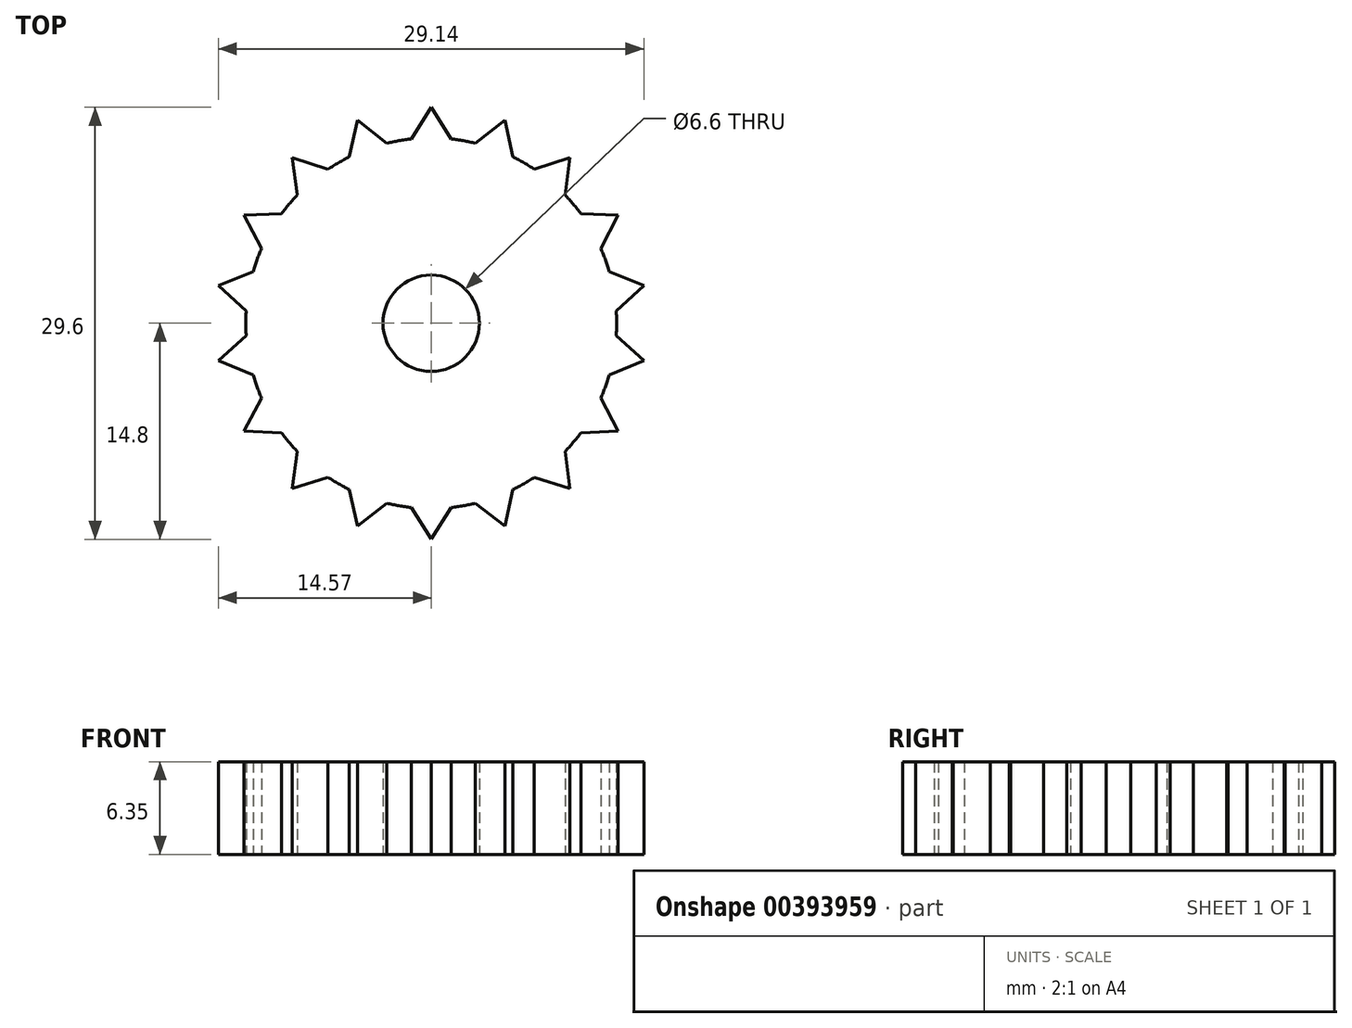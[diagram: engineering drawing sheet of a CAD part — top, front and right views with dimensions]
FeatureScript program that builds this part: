
annotation { "Feature Type Name" : "Feature", "Feature Type Description" : "" }
export const myFeature = defineFeature(function(context is Context, id is Id, definition is map)
    precondition{}
    {
        {
            var Q0;
            Q0=qCreatedBy(makeId("Top.planeOp"),FACE);
            var sketch = newSketch(context, id + "F0", { "sketchPlane" : qUnion([Q0])});
            skCircle(sketch, "E0", {"center": v(0, 0) * mm, "radius": 12.7 * mm});
            skCircle(sketch, "E1", {"center": v(0, 0) * mm, "radius": 3.3 * mm});
            skLineSegment(sketch, "E2", {"start": v(0, 12.7) * mm, "end": v(0, 14.8) * mm});
            skLineSegment(sketch, "E3", {"start": v(0, 14.8) * mm, "end": v(-1.37, 12.63) * mm});
            skLineSegment(sketch, "E4", {"start": v(0, 14.8) * mm, "end": v(1.37, 12.63) * mm});
            skLineSegment(sketch, "E5.1.0", {"start": v(-5.06, 13.9) * mm, "end": v(-5.6, 11.4) * mm});
            skLineSegment(sketch, "E5.1.1", {"start": v(-5.06, 13.9) * mm, "end": v(-3.03, 12.33) * mm});
            skLineSegment(sketch, "E5.2.0", {"start": v(-9.51, 11.33) * mm, "end": v(-9.16, 8.8) * mm});
            skLineSegment(sketch, "E5.2.1", {"start": v(-9.51, 11.33) * mm, "end": v(-7.07, 10.55) * mm});
            skLineSegment(sketch, "E5.3.0", {"start": v(-12.81, 7.4) * mm, "end": v(-11.62, 5.13) * mm});
            skLineSegment(sketch, "E5.3.1", {"start": v(-12.81, 7.4) * mm, "end": v(-10.25, 7.5) * mm});
            skLineSegment(sketch, "E5.4.0", {"start": v(-14.57, 2.57) * mm, "end": v(-12.67, 0.84) * mm});
            skLineSegment(sketch, "E5.4.1", {"start": v(-14.57, 2.57) * mm, "end": v(-12.2, 3.54) * mm});
            skLineSegment(sketch, "E5.5.0", {"start": v(-14.57, -2.57) * mm, "end": v(-12.2, -3.54) * mm});
            skLineSegment(sketch, "E5.5.1", {"start": v(-14.57, -2.57) * mm, "end": v(-12.67, -0.84) * mm});
            skLineSegment(sketch, "E5.6.0", {"start": v(-12.81, -7.4) * mm, "end": v(-10.25, -7.5) * mm});
            skLineSegment(sketch, "E5.6.1", {"start": v(-12.81, -7.4) * mm, "end": v(-11.62, -5.13) * mm});
            skLineSegment(sketch, "E5.7.0", {"start": v(-9.51, -11.33) * mm, "end": v(-7.07, -10.55) * mm});
            skLineSegment(sketch, "E5.7.1", {"start": v(-9.51, -11.33) * mm, "end": v(-9.16, -8.8) * mm});
            skLineSegment(sketch, "E5.8.0", {"start": v(-5.06, -13.9) * mm, "end": v(-3.03, -12.33) * mm});
            skLineSegment(sketch, "E5.8.1", {"start": v(-5.06, -13.9) * mm, "end": v(-5.6, -11.4) * mm});
            skLineSegment(sketch, "E5.9.0", {"start": v(0, -14.8) * mm, "end": v(1.37, -12.63) * mm});
            skLineSegment(sketch, "E5.9.1", {"start": v(0, -14.8) * mm, "end": v(-1.37, -12.63) * mm});
            skLineSegment(sketch, "E5.10.0", {"start": v(5.06, -13.9) * mm, "end": v(5.6, -11.4) * mm});
            skLineSegment(sketch, "E5.10.1", {"start": v(5.06, -13.9) * mm, "end": v(3.03, -12.33) * mm});
            skLineSegment(sketch, "E5.11.0", {"start": v(9.51, -11.33) * mm, "end": v(9.16, -8.8) * mm});
            skLineSegment(sketch, "E5.11.1", {"start": v(9.51, -11.33) * mm, "end": v(7.07, -10.55) * mm});
            skLineSegment(sketch, "E5.12.0", {"start": v(12.81, -7.4) * mm, "end": v(11.62, -5.13) * mm});
            skLineSegment(sketch, "E5.12.1", {"start": v(12.81, -7.4) * mm, "end": v(10.25, -7.5) * mm});
            skLineSegment(sketch, "E5.13.0", {"start": v(14.57, -2.57) * mm, "end": v(12.67, -0.84) * mm});
            skLineSegment(sketch, "E5.13.1", {"start": v(14.57, -2.57) * mm, "end": v(12.2, -3.54) * mm});
            skLineSegment(sketch, "E5.14.0", {"start": v(14.57, 2.57) * mm, "end": v(12.2, 3.54) * mm});
            skLineSegment(sketch, "E5.14.1", {"start": v(14.57, 2.57) * mm, "end": v(12.67, 0.84) * mm});
            skLineSegment(sketch, "E5.15.0", {"start": v(12.81, 7.4) * mm, "end": v(10.25, 7.5) * mm});
            skLineSegment(sketch, "E5.15.1", {"start": v(12.81, 7.4) * mm, "end": v(11.62, 5.13) * mm});
            skLineSegment(sketch, "E5.16.0", {"start": v(9.51, 11.33) * mm, "end": v(7.07, 10.55) * mm});
            skLineSegment(sketch, "E5.16.1", {"start": v(9.51, 11.33) * mm, "end": v(9.16, 8.8) * mm});
            skLineSegment(sketch, "E5.17.0", {"start": v(5.06, 13.9) * mm, "end": v(3.03, 12.33) * mm});
            skLineSegment(sketch, "E5.17.1", {"start": v(5.06, 13.9) * mm, "end": v(5.6, 11.4) * mm});
            skSolve(sketch);
        }
        {
            var Q0;
            Q0 = qSketchRegion(id + "F0", true);
            extrude(context, id + "F1", {"entities" : qUnion([Q0]), "depth" : 6.35 * mm});
        }
    });
